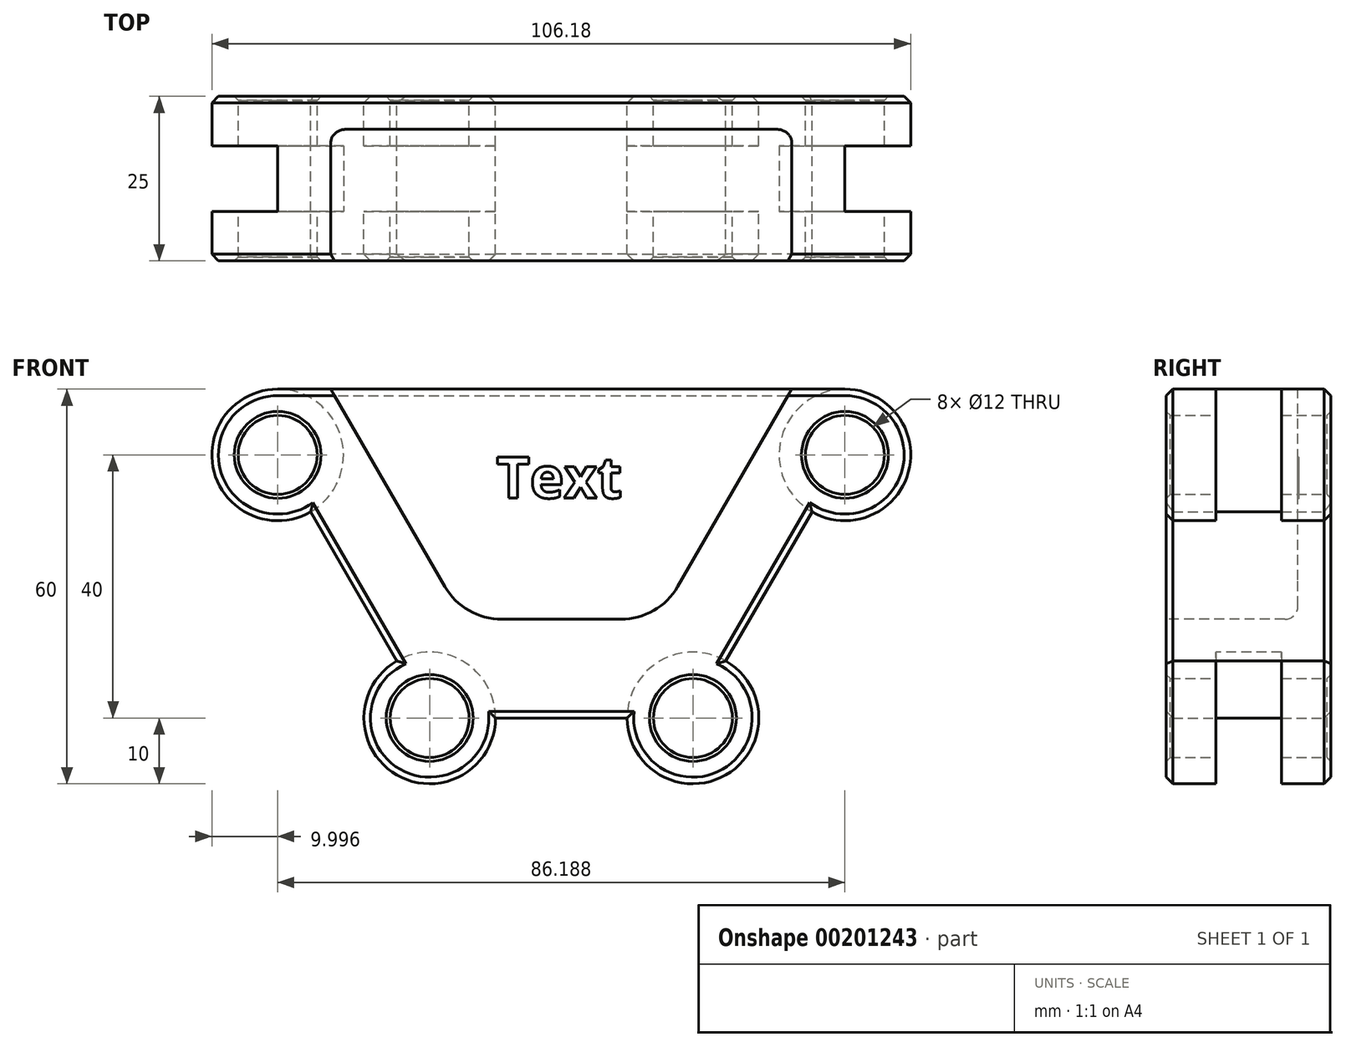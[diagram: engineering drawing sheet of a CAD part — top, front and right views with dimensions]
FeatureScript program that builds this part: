
annotation { "Feature Type Name" : "Feature", "Feature Type Description" : "" }
export const myFeature = defineFeature(function(context is Context, id is Id, definition is map)
    precondition{}
    {
        {
            var Q0;
            Q0=qCreatedBy(makeId("Front.planeOp"),FACE);
            var sketch = newSketch(context, id + "F0", { "sketchPlane" : qUnion([Q0])});
            skLineSegment(sketch, "E0", {"start": v(-43.1, 40) * mm, "end": v(-20, 0) * mm});
            skLineSegment(sketch, "E1", {"start": v(-20, 0) * mm, "end": v(20, 0) * mm});
            skLineSegment(sketch, "E2", {"start": v(20, 0) * mm, "end": v(43.1, 40) * mm});
            skLineSegment(sketch, "E3", {"start": v(0, 0) * mm, "end": v(0, -8.93) * mm, "construction": true});
            skLineSegment(sketch, "E4", {"start": v(0, -8.93) * mm, "end": v(0, 44.2) * mm, "construction": true});
            skCircle(sketch, "E5", {"center": v(-20, 0) * mm, "radius": 6 * mm});
            skCircle(sketch, "E6", {"center": v(20, 0) * mm, "radius": 6 * mm});
            skCircle(sketch, "E7", {"center": v(43.1, 40) * mm, "radius": 6 * mm});
            skCircle(sketch, "E8", {"center": v(-43.1, 40) * mm, "radius": 6 * mm});
            skCircle(sketch, "E9", {"center": v(-20, 0) * mm, "radius": 10 * mm});
            skCircle(sketch, "E10", {"center": v(20, 0) * mm, "radius": 10 * mm});
            skCircle(sketch, "E11", {"center": v(43.1, 40) * mm, "radius": 10 * mm});
            skCircle(sketch, "E12", {"center": v(-43.1, 40) * mm, "radius": 10 * mm});
            skLineSegment(sketch, "E13", {"start": v(-43.1, 50) * mm, "end": v(43.1, 50) * mm});
            skSolve(sketch);
        }
        {
            var Q0;
            Q0=makeQuery(id+"F0.imprint","IMPRINT",FACE,{"disambiguationData":[TD([[makeQuery(id+"F0.imprint","IMPRINT",EDGE,{"derivedFrom":sQuery(id+"F0.wireOp",EDGE,"E8")}),-1.0]])]});
            var Q1;
            Q1=makeQuery(id+"F0.imprint","IMPRINT",FACE,{"disambiguationData":[TD([[makeQuery(id+"F0.imprint","IMPRINT",EDGE,{"derivedFrom":sQuery(id+"F0.wireOp",EDGE,"E7")}),-1.0]])]});
            var Q2;
            {var subQ0=sQuery(id+"F0.wireOp",EDGE,"E10");var subQ1=sQuery(id+"F0.wireOp",EDGE,"E1");var subQ2=makeQuery(id+"F0.imprint","INTERSECT",VERTEX,{"derivedFrom":[subQ1,subQ0]});Q2=makeQuery(id+"F0.imprint","IMPRINT",FACE,{"disambiguationData":[TD([[makeQuery(id+"F0.imprint","IMPRINT",EDGE,{"disambiguationData":[TD([[subQ2,-1.0]])],"derivedFrom":subQ1}),-1.0]])]});}
            var Q3;
            {var subQ0=sQuery(id+"F0.wireOp",EDGE,"E9");var subQ1=sQuery(id+"F0.wireOp",EDGE,"E0");var subQ2=makeQuery(id+"F0.imprint","INTERSECT",VERTEX,{"derivedFrom":[subQ1,subQ0]});Q3=makeQuery(id+"F0.imprint","IMPRINT",FACE,{"disambiguationData":[TD([[makeQuery(id+"F0.imprint","IMPRINT",EDGE,{"disambiguationData":[TD([[subQ2,-1.0]])],"derivedFrom":subQ1}),-1.0]])]});}
            var Q4;
            {var subQ0=sQuery(id+"F0.wireOp",EDGE,"E10");var subQ1=sQuery(id+"F0.wireOp",EDGE,"E1");var subQ2=makeQuery(id+"F0.imprint","INTERSECT",VERTEX,{"derivedFrom":[subQ1,subQ0]});Q4=makeQuery(id+"F0.imprint","IMPRINT",FACE,{"disambiguationData":[TD([[makeQuery(id+"F0.imprint","IMPRINT",EDGE,{"disambiguationData":[TD([[subQ2,-1.0]])],"derivedFrom":subQ1}),1.0]])]});}
            var Q5;
            {var subQ0=sQuery(id+"F0.wireOp",EDGE,"E9");var subQ1=sQuery(id+"F0.wireOp",EDGE,"E0");var subQ2=makeQuery(id+"F0.imprint","INTERSECT",VERTEX,{"derivedFrom":[subQ1,subQ0]});Q5=makeQuery(id+"F0.imprint","IMPRINT",FACE,{"disambiguationData":[TD([[makeQuery(id+"F0.imprint","IMPRINT",EDGE,{"disambiguationData":[TD([[subQ2,-1.0]])],"derivedFrom":subQ1}),1.0]])]});}
            var Q6;
            {var subQ11=sQuery(id+"F0.wireOp",EDGE,"E13");Q6=makeQuery(id+"F0.imprint","IMPRINT",FACE,{"disambiguationData":[TD([[makeQuery(id+"F0.imprint","IMPRINT",EDGE,{"derivedFrom":subQ11}),-1.0]])]});}
            extrude(context, id + "F1", {"entities" : qUnion([Q0, Q1, Q2, Q3, Q4, Q5, Q6]), "depth" : 25 * mm, "symmetric" : true});
        }
        {
            var Q0;
            Q0=makeQuery(id+"F0.imprint","IMPRINT",FACE,{"disambiguationData":[TD([[makeQuery(id+"F0.imprint","IMPRINT",EDGE,{"derivedFrom":sQuery(id+"F0.wireOp",EDGE,"E8")}),-1.0]])]});
            var Q1;
            Q1=makeQuery(id+"F0.imprint","IMPRINT",FACE,{"disambiguationData":[TD([[makeQuery(id+"F0.imprint","IMPRINT",EDGE,{"derivedFrom":sQuery(id+"F0.wireOp",EDGE,"E7")}),-1.0]])]});
            var Q2;
            {var subQ0=sQuery(id+"F0.wireOp",EDGE,"E10");var subQ1=sQuery(id+"F0.wireOp",EDGE,"E1");var subQ2=makeQuery(id+"F0.imprint","INTERSECT",VERTEX,{"derivedFrom":[subQ1,subQ0]});Q2=makeQuery(id+"F0.imprint","IMPRINT",FACE,{"disambiguationData":[TD([[makeQuery(id+"F0.imprint","IMPRINT",EDGE,{"disambiguationData":[TD([[subQ2,-1.0]])],"derivedFrom":subQ1}),-1.0]])]});}
            var Q3;
            {var subQ0=sQuery(id+"F0.wireOp",EDGE,"E10");var subQ1=sQuery(id+"F0.wireOp",EDGE,"E1");var subQ2=makeQuery(id+"F0.imprint","INTERSECT",VERTEX,{"derivedFrom":[subQ1,subQ0]});Q3=makeQuery(id+"F0.imprint","IMPRINT",FACE,{"disambiguationData":[TD([[makeQuery(id+"F0.imprint","IMPRINT",EDGE,{"disambiguationData":[TD([[subQ2,-1.0]])],"derivedFrom":subQ1}),1.0]])]});}
            var Q4;
            {var subQ0=sQuery(id+"F0.wireOp",EDGE,"E9");var subQ1=sQuery(id+"F0.wireOp",EDGE,"E0");var subQ2=makeQuery(id+"F0.imprint","INTERSECT",VERTEX,{"derivedFrom":[subQ1,subQ0]});Q4=makeQuery(id+"F0.imprint","IMPRINT",FACE,{"disambiguationData":[TD([[makeQuery(id+"F0.imprint","IMPRINT",EDGE,{"disambiguationData":[TD([[subQ2,-1.0]])],"derivedFrom":subQ1}),-1.0]])]});}
            var Q5;
            {var subQ0=sQuery(id+"F0.wireOp",EDGE,"E9");var subQ1=sQuery(id+"F0.wireOp",EDGE,"E0");var subQ2=makeQuery(id+"F0.imprint","INTERSECT",VERTEX,{"derivedFrom":[subQ1,subQ0]});Q5=makeQuery(id+"F0.imprint","IMPRINT",FACE,{"disambiguationData":[TD([[makeQuery(id+"F0.imprint","IMPRINT",EDGE,{"disambiguationData":[TD([[subQ2,-1.0]])],"derivedFrom":subQ1}),1.0]])]});}
            extrude(context, id + "F2", {"entities" : qUnion([Q0, Q1, Q2, Q3, Q4, Q5]), "operationType" : NewBodyOperationType.REMOVE, "oppositeDirection" : true, "depth" : 10 * mm, "symmetric" : true});
        }
        {
            var Q0;
            Q0=makeQuery(id+"F1.opExtrude","CAP_FACE",FACE,{"disambiguationData":[OSD([sQuery(id+"F0.wireOp",EDGE,"E0"),sQuery(id+"F0.wireOp",EDGE,"E1"),sQuery(id+"F0.wireOp",EDGE,"E2"),sQuery(id+"F0.wireOp",EDGE,"E5"),sQuery(id+"F0.wireOp",EDGE,"E6"),sQuery(id+"F0.wireOp",EDGE,"E7"),sQuery(id+"F0.wireOp",EDGE,"E8"),sQuery(id+"F0.wireOp",EDGE,"E9"),sQuery(id+"F0.wireOp",EDGE,"E10"),sQuery(id+"F0.wireOp",EDGE,"E11"),sQuery(id+"F0.wireOp",EDGE,"E12"),sQuery(id+"F0.wireOp",EDGE,"E13")])],"isStart":false});
            var sketch = newSketch(context, id + "F3", { "sketchPlane" : qUnion([Q0])});
            skLineSegment(sketch, "E14", {"start": v(-35.01, 50) * mm, "end": v(-17.7, 20) * mm});
            skLineSegment(sketch, "E15", {"start": v(-9.03, 15) * mm, "end": v(9.03, 15) * mm});
            skLineSegment(sketch, "E16", {"start": v(17.7, 20) * mm, "end": v(35.01, 50) * mm});
            skLineSegment(sketch, "E17", {"start": v(0, -6.35) * mm, "end": v(0, 23.92) * mm, "construction": true});
            skPoint(sketch, "E18.visualSharp", {"position": v(-14.8, 15) * mm});
            skArc(sketch, "E18.filletArc", {"start": v(-17.7, 20) * mm, "mid": v(-14.03, 16.34) * mm, "end": v(-9.03, 15) * mm});
            skPoint(sketch, "E19.visualSharp", {"position": v(14.8, 15) * mm});
            skArc(sketch, "E19.filletArc", {"start": v(9.03, 15) * mm, "mid": v(14.03, 16.34) * mm, "end": v(17.7, 20) * mm});
            skSolve(sketch);
        }
        {
            var Q0;
            {var subQ1=sQuery(id+"F3.wireOp",EDGE,"E14");Q0=makeQuery(id+"F3.imprint","IMPRINT",FACE,{"disambiguationData":[TD([[makeQuery(id+"F3.imprint","IMPRINT",EDGE,{"derivedFrom":subQ1}),1.0]])]});}
            extrude(context, id + "F4", {"entities" : qUnion([Q0]), "operationType" : NewBodyOperationType.REMOVE, "oppositeDirection" : true, "depth" : 20 * mm});
        }
        {
            var Q0;
            Q0=makeQuery(id+"F4.boolean.opBoolean","COPY",EDGE,{"derivedFrom":makeQuery(id+"F4.opExtrude","CAP_EDGE",EDGE,{"disambiguationData":[OSD([sQuery(id+"F3.wireOp",EDGE,"E14")])],"isStart":false})});
            fillet(context, id + "F5", {"entities" : qUnion([Q0]), "radius" : 2 * mm, "tangentPropagation" : true, "allowEdgeOverflow" : false});
        }
        {
            var Q0;
            Q0=makeQuery(id+"F4.boolean.opBoolean","COPY",EDGE,{"derivedFrom":makeQuery(id+"F4.opExtrude","CAP_EDGE",EDGE,{"disambiguationData":[OSD([sQuery(id+"F3.wireOp",EDGE,"E14")])],"isStart":true})});
            var Q1;
            {var subQ0=sQuery(id+"F0.wireOp",EDGE,"E13");var subQ1=sQuery(id+"F0.wireOp",EDGE,"E12");Q1=makeQuery(id+"F4.boolean.opBoolean","SPLIT",EDGE,{"disambiguationData":[TD([makeQuery(id+"F1.opExtrude","SWEPT_FACE",FACE,{"disambiguationData":[OSD([subQ1])]})])],"derivedFrom":makeQuery(id+"F1.opExtrude","CAP_EDGE",EDGE,{"disambiguationData":[OSD([subQ0])],"isStart":false})});}
            var Q2;
            Q2=makeQuery(id+"F1.opExtrude","CAP_EDGE",EDGE,{"disambiguationData":[OSD([sQuery(id+"F0.wireOp",EDGE,"E0")])],"isStart":false});
            var Q3;
            Q3=makeQuery(id+"F1.opExtrude","CAP_EDGE",EDGE,{"disambiguationData":[OSD([sQuery(id+"F0.wireOp",EDGE,"E9")])],"isStart":false});
            var Q4;
            {var subQ0=sQuery(id+"F0.wireOp",EDGE,"E13");var subQ1=sQuery(id+"F0.wireOp",EDGE,"E11");Q4=makeQuery(id+"F4.boolean.opBoolean","SPLIT",EDGE,{"disambiguationData":[TD([makeQuery(id+"F1.opExtrude","SWEPT_FACE",FACE,{"disambiguationData":[OSD([subQ1])]})])],"derivedFrom":makeQuery(id+"F1.opExtrude","CAP_EDGE",EDGE,{"disambiguationData":[OSD([subQ0])],"isStart":false})});}
            var Q5;
            Q5=makeQuery(id+"F1.opExtrude","CAP_EDGE",EDGE,{"disambiguationData":[OSD([sQuery(id+"F0.wireOp",EDGE,"E2")])],"isStart":false});
            var Q6;
            Q6=makeQuery(id+"F1.opExtrude","CAP_EDGE",EDGE,{"disambiguationData":[OSD([sQuery(id+"F0.wireOp",EDGE,"E10")])],"isStart":false});
            var Q7;
            Q7=makeQuery(id+"F1.opExtrude","CAP_EDGE",EDGE,{"disambiguationData":[OSD([sQuery(id+"F0.wireOp",EDGE,"E1")])],"isStart":false});
            var Q8;
            Q8=makeQuery(id+"F1.opExtrude","CAP_EDGE",EDGE,{"disambiguationData":[OSD([sQuery(id+"F0.wireOp",EDGE,"E11")])],"isStart":true});
            var Q9;
            Q9=makeQuery(id+"F1.opExtrude","CAP_EDGE",EDGE,{"disambiguationData":[OSD([sQuery(id+"F0.wireOp",EDGE,"E10")])],"isStart":true});
            var Q10;
            Q10=makeQuery(id+"F1.opExtrude","CAP_EDGE",EDGE,{"disambiguationData":[OSD([sQuery(id+"F0.wireOp",EDGE,"E2")])],"isStart":true});
            var Q11;
            Q11=makeQuery(id+"F1.opExtrude","CAP_EDGE",EDGE,{"disambiguationData":[OSD([sQuery(id+"F0.wireOp",EDGE,"E1")])],"isStart":true});
            var Q12;
            Q12=makeQuery(id+"F1.opExtrude","CAP_EDGE",EDGE,{"disambiguationData":[OSD([sQuery(id+"F0.wireOp",EDGE,"E9")])],"isStart":true});
            var Q13;
            Q13=makeQuery(id+"F1.opExtrude","CAP_EDGE",EDGE,{"disambiguationData":[OSD([sQuery(id+"F0.wireOp",EDGE,"E0")])],"isStart":true});
            chamfer(context, id + "F6", {"entities" : qUnion([Q0, Q1, Q2, Q3, Q4, Q5, Q6, Q7, Q8, Q9, Q10, Q11, Q12, Q13]), "width" : 1 * mm, "tangentPropagation" : true});
        }
        {
            var Q0;
            Q0=makeQuery(id+"F1.opExtrude","CAP_EDGE",EDGE,{"disambiguationData":[OSD([sQuery(id+"F0.wireOp",EDGE,"E7")])],"isStart":false});
            var Q1;
            Q1=makeQuery(id+"F1.opExtrude","CAP_EDGE",EDGE,{"disambiguationData":[OSD([sQuery(id+"F0.wireOp",EDGE,"E6")])],"isStart":false});
            var Q2;
            Q2=makeQuery(id+"F1.opExtrude","CAP_EDGE",EDGE,{"disambiguationData":[OSD([sQuery(id+"F0.wireOp",EDGE,"E5")])],"isStart":false});
            var Q3;
            Q3=makeQuery(id+"F1.opExtrude","CAP_EDGE",EDGE,{"disambiguationData":[OSD([sQuery(id+"F0.wireOp",EDGE,"E8")])],"isStart":false});
            var Q4;
            Q4=makeQuery(id+"F1.opExtrude","CAP_EDGE",EDGE,{"disambiguationData":[OSD([sQuery(id+"F0.wireOp",EDGE,"E8")])],"isStart":true});
            var Q5;
            Q5=makeQuery(id+"F1.opExtrude","CAP_EDGE",EDGE,{"disambiguationData":[OSD([sQuery(id+"F0.wireOp",EDGE,"E5")])],"isStart":true});
            var Q6;
            Q6=makeQuery(id+"F1.opExtrude","CAP_EDGE",EDGE,{"disambiguationData":[OSD([sQuery(id+"F0.wireOp",EDGE,"E6")])],"isStart":true});
            var Q7;
            Q7=makeQuery(id+"F1.opExtrude","CAP_EDGE",EDGE,{"disambiguationData":[OSD([sQuery(id+"F0.wireOp",EDGE,"E7")])],"isStart":true});
            chamfer(context, id + "F7", {"entities" : qUnion([Q0, Q1, Q2, Q3, Q4, Q5, Q6, Q7]), "width" : 0.6 * mm, "tangentPropagation" : true});
        }
        {
            var Q0;
            Q0=makeQuery(id+"F4.boolean.opBoolean","COPY",FACE,{"derivedFrom":makeQuery(id+"F4.opExtrude","CAP_FACE",FACE,{"disambiguationData":[OSD([sQuery(id+"F0.wireOp",EDGE,"E13"),sQuery(id+"F3.wireOp",EDGE,"E14"),sQuery(id+"F3.wireOp",EDGE,"E15"),sQuery(id+"F3.wireOp",EDGE,"E16"),sQuery(id+"F3.wireOp",EDGE,"E18.filletArc"),sQuery(id+"F3.wireOp",EDGE,"E19.filletArc")])],"isStart":false})});
            var sketch = newSketch(context, id + "F8", { "sketchPlane" : qUnion([Q0])});
            skText(sketch, "E20", { "text": "Text", "fontName": "OpenSans-Bold.ttf"});
            const initialGuessF8  = {"E20": [-0.00985, 0.03343, 1, 0, 0.0063]};
            skSetInitialGuess(sketch, initialGuessF8);
            skSolve(sketch);
        }
        {
            var Q0;
            Q0=qSketchRegion(id+"F8",true);
            extrude(context, id + "F9", {"entities" : qUnion([Q0]), "operationType" : NewBodyOperationType.REMOVE, "oppositeDirection" : true, "depth" : 0.1 * mm});
        }
    });
